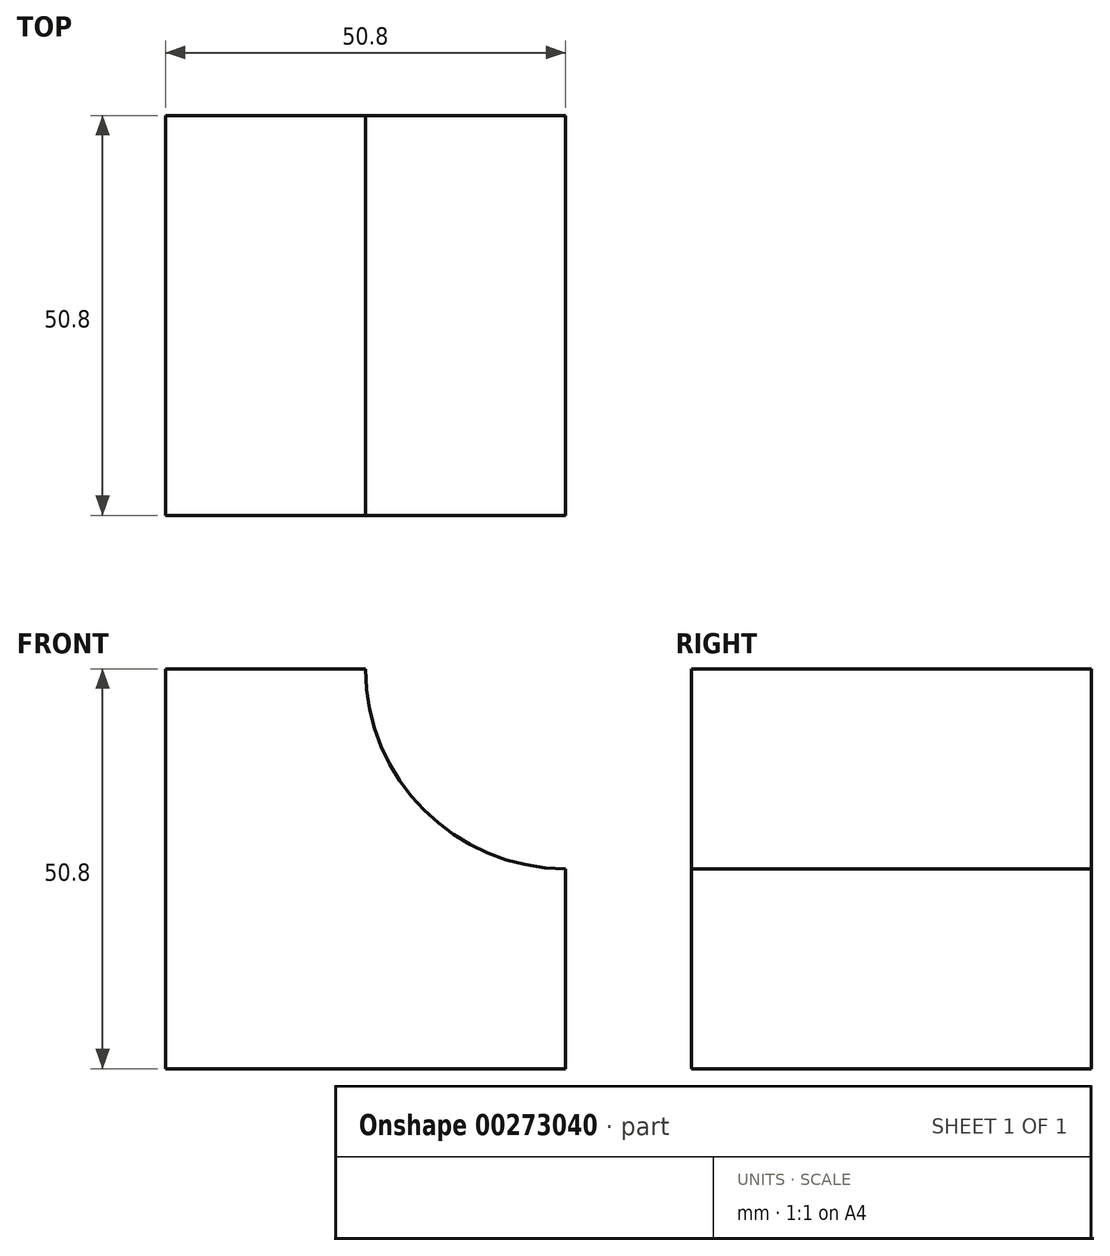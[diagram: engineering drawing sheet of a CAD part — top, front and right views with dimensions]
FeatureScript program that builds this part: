
annotation { "Feature Type Name" : "Feature", "Feature Type Description" : "" }
export const myFeature = defineFeature(function(context is Context, id is Id, definition is map)
    precondition{}
    {
        {
            var Q0;
            Q0=qCreatedBy(makeId("Front.planeOp"),FACE);
            var sketch = newSketch(context, id + "F0", { "sketchPlane" : qUnion([Q0])});
            skLineSegment(sketch, "E0", {"start": v(0, 0) * mm, "end": v(-50.8, 0) * mm});
            skLineSegment(sketch, "E1", {"start": v(-50.8, 0) * mm, "end": v(-50.8, 50.8) * mm});
            skLineSegment(sketch, "E2", {"start": v(-50.8, 50.8) * mm, "end": v(-25.4, 50.8) * mm});
            skLineSegment(sketch, "E3", {"start": v(-25.4, 50.8) * mm, "end": v(-25.4, 25.4) * mm});
            skLineSegment(sketch, "E4", {"start": v(-25.4, 25.4) * mm, "end": v(0, 25.4) * mm});
            skLineSegment(sketch, "E5", {"start": v(0, 25.4) * mm, "end": v(0, 0) * mm});
            skArc(sketch, "E6", {"start": v(-25.4, 50.8) * mm, "mid": v(-17.96, 32.84) * mm, "end": v(0, 25.4) * mm});
            skSolve(sketch);
        }
        {
            var Q0;
            Q0=makeQuery(id+"F0.imprint","IMPRINT",FACE,{"disambiguationData":[TD([[makeQuery(id+"F0.imprint","IMPRINT",EDGE,{"derivedFrom":sQuery(id+"F0.wireOp",EDGE,"E0")}),-1.0]])]});
            var Q1;
            Q1=makeQuery(id+"F0.imprint","IMPRINT",FACE,{"disambiguationData":[TD([[makeQuery(id+"F0.imprint","IMPRINT",EDGE,{"derivedFrom":sQuery(id+"F0.wireOp",EDGE,"E3")}),1.0]])]});
            extrude(context, id + "F1", {"entities" : qUnion([Q0, Q1]), "depth" : 50.8 * mm});
        }
    });
